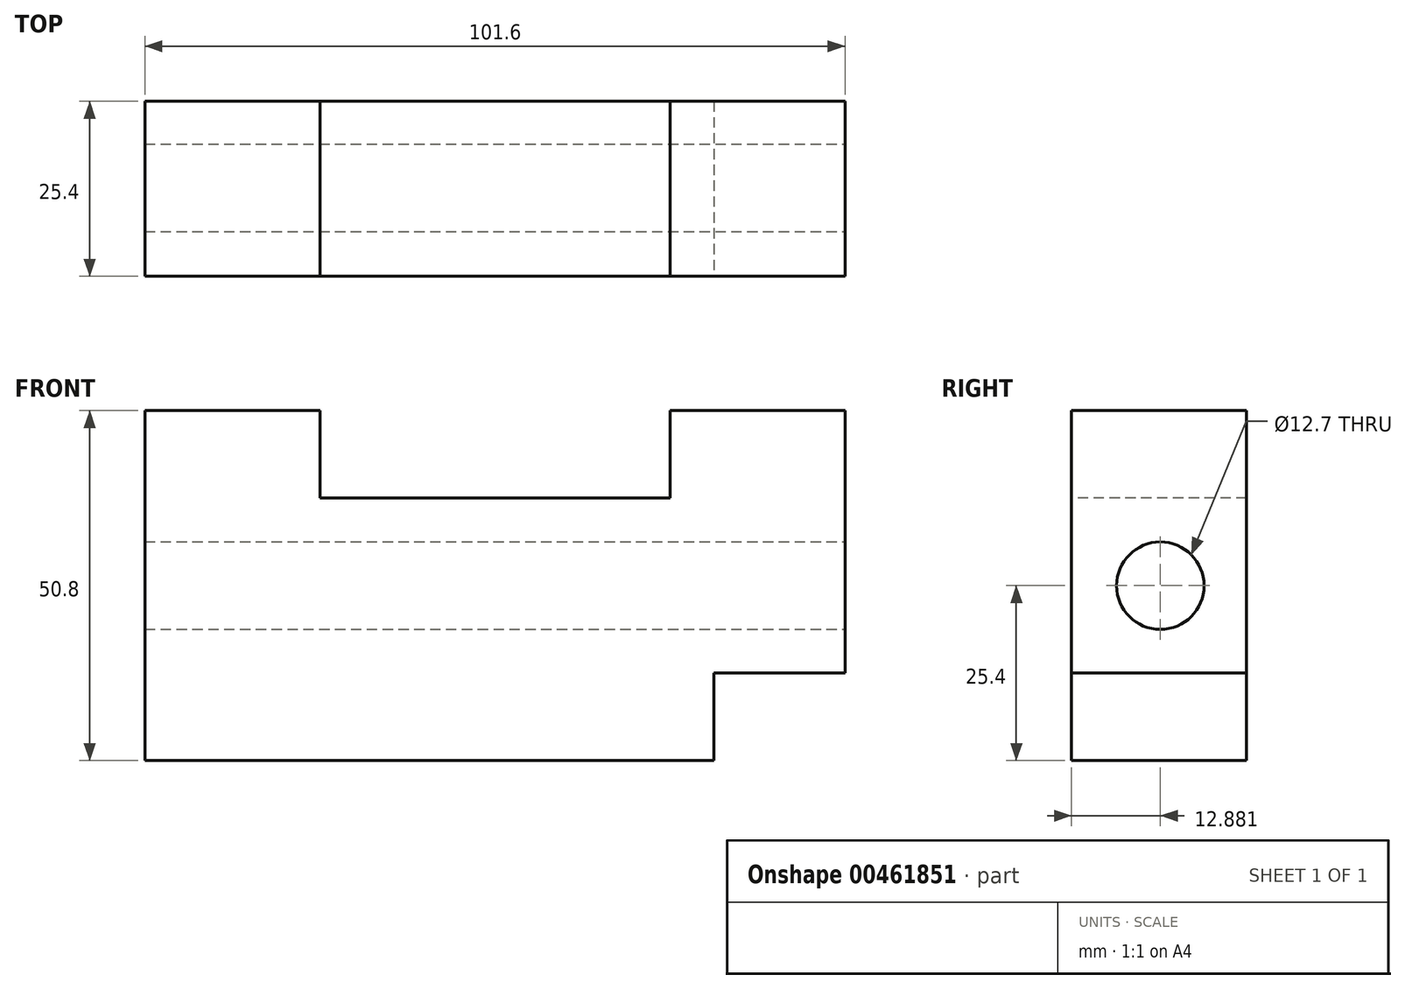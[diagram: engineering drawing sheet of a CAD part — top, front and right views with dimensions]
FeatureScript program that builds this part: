
annotation { "Feature Type Name" : "Feature", "Feature Type Description" : "" }
export const myFeature = defineFeature(function(context is Context, id is Id, definition is map)
    precondition{}
    {
        {
            var Q0;
            Q0=qCreatedBy(makeId("Front.planeOp"),FACE);
            var sketch = newSketch(context, id + "F0", { "sketchPlane" : qUnion([Q0])});
            skLineSegment(sketch, "E0.bottom", {"start": v(50.8, 25.4) * mm, "end": v(-50.8, 25.4) * mm});
            skLineSegment(sketch, "E0.top", {"start": v(50.8, -25.4) * mm, "end": v(-50.8, -25.4) * mm});
            skLineSegment(sketch, "E0.left", {"start": v(50.8, 25.4) * mm, "end": v(50.8, -25.4) * mm});
            skLineSegment(sketch, "E0.right", {"start": v(-50.8, 25.4) * mm, "end": v(-50.8, -25.4) * mm});
            skPoint(sketch, "E0.middle", {"position": v(0, 0) * mm});
            skSolve(sketch);
        }
        {
            var Q0;
            Q0 = qSketchRegion(id + "F0", true);
            extrude(context, id + "F1", {"entities" : qUnion([Q0]), "depth" : 25.4 * mm});
        }
        {
            var Q0;
            Q0=makeQuery(id+"F1.opExtrude","CAP_FACE",FACE,{"disambiguationData":[OSD([sQuery(id+"F0.wireOp",EDGE,"E0.bottom"),sQuery(id+"F0.wireOp",EDGE,"E0.top"),sQuery(id+"F0.wireOp",EDGE,"E0.left"),sQuery(id+"F0.wireOp",EDGE,"E0.right")])],"isStart":false});
            var sketch = newSketch(context, id + "F2", { "sketchPlane" : qUnion([Q0])});
            skLineSegment(sketch, "E1.bottom", {"start": v(-25.4, 25.4) * mm, "end": v(25.4, 25.4) * mm});
            skLineSegment(sketch, "E1.top", {"start": v(-25.4, 12.7) * mm, "end": v(25.4, 12.7) * mm});
            skLineSegment(sketch, "E1.left", {"start": v(-25.4, 25.4) * mm, "end": v(-25.4, 12.7) * mm});
            skLineSegment(sketch, "E1.right", {"start": v(25.4, 25.4) * mm, "end": v(25.4, 12.7) * mm});
            skSolve(sketch);
        }
        {
            var Q0;
            Q0 = qSketchRegion(id + "F2", true);
            extrude(context, id + "F3", {"entities" : qUnion([Q0]), "operationType" : NewBodyOperationType.REMOVE, "endBound" : BoundingType.THROUGH_ALL, "oppositeDirection" : true, "depth" : 25.4 * mm});
        }
        {
            var Q0;
            Q0=makeQuery(id+"F1.opExtrude","CAP_FACE",FACE,{"disambiguationData":[OSD([sQuery(id+"F0.wireOp",EDGE,"E0.bottom"),sQuery(id+"F0.wireOp",EDGE,"E0.top"),sQuery(id+"F0.wireOp",EDGE,"E0.left"),sQuery(id+"F0.wireOp",EDGE,"E0.right")])],"isStart":false});
            var sketch = newSketch(context, id + "F4", { "sketchPlane" : qUnion([Q0])});
            skLineSegment(sketch, "E2.bottom", {"start": v(31.75, -25.4) * mm, "end": v(50.8, -25.4) * mm});
            skLineSegment(sketch, "E2.top", {"start": v(31.75, -12.7) * mm, "end": v(50.8, -12.7) * mm});
            skLineSegment(sketch, "E2.left", {"start": v(31.75, -25.4) * mm, "end": v(31.75, -12.7) * mm});
            skLineSegment(sketch, "E2.right", {"start": v(50.8, -25.4) * mm, "end": v(50.8, -12.7) * mm});
            skSolve(sketch);
        }
        {
            var Q0;
            Q0 = qSketchRegion(id + "F4", true);
            extrude(context, id + "F5", {"entities" : qUnion([Q0]), "operationType" : NewBodyOperationType.REMOVE, "endBound" : BoundingType.THROUGH_ALL, "oppositeDirection" : true, "depth" : 25.4 * mm});
        }
        {
            var Q0;
            Q0=makeQuery(id+"F1.opExtrude","SWEPT_FACE",FACE,{"disambiguationData":[OSD([sQuery(id+"F0.wireOp",EDGE,"E0.left")])]});
            var sketch = newSketch(context, id + "F6", { "sketchPlane" : qUnion([Q0])});
            skCircle(sketch, "E3", {"center": v(-12.52, 0) * mm, "radius": 6.35 * mm});
            skSolve(sketch);
        }
        {
            var Q0;
            Q0 = qSketchRegion(id + "F6", true);
            extrude(context, id + "F7", {"entities" : qUnion([Q0]), "operationType" : NewBodyOperationType.REMOVE, "endBound" : BoundingType.THROUGH_ALL, "oppositeDirection" : true, "depth" : 25.4 * mm});
        }
    });
